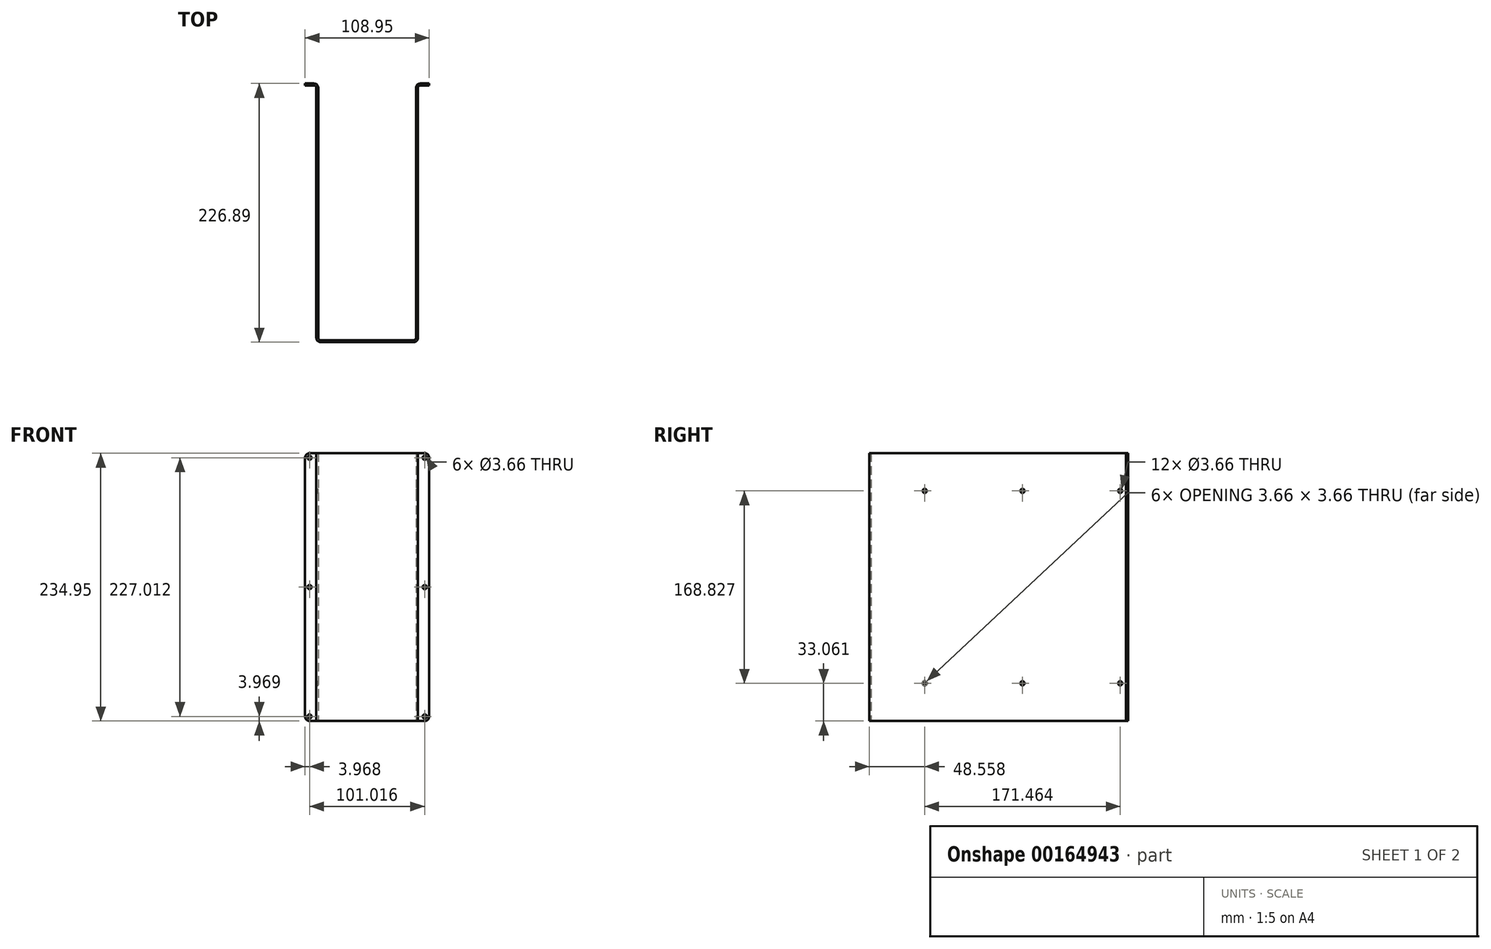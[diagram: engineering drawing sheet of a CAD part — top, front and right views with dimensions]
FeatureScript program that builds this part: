
annotation { "Feature Type Name" : "Feature", "Feature Type Description" : "" }
export const myFeature = defineFeature(function(context is Context, id is Id, definition is map)
    precondition{}
    {
        {
            var Q0;
            Q0=qCreatedBy(makeId("Top.planeOp"),FACE);
            var sketch = newSketch(context, id + "F0", { "sketchPlane" : qUnion([Q0])});
            skLineSegment(sketch, "E0", {"start": v(0, 0) * mm, "end": v(-11.63, 0) * mm});
            skLineSegment(sketch, "E1", {"start": v(0, 0) * mm, "end": v(0, -225.18) * mm});
            skLineSegment(sketch, "E2", {"start": v(0, -225.18) * mm, "end": v(85.7, -225.18) * mm});
            skLineSegment(sketch, "E3", {"start": v(87.4, -226.9) * mm, "end": v(-1.7, -226.9) * mm});
            skLineSegment(sketch, "E4", {"start": v(-1.7, -226.9) * mm, "end": v(-1.7, -1.7) * mm});
            skLineSegment(sketch, "E5", {"start": v(0, -225.18) * mm, "end": v(-1.7, -225.18) * mm, "construction": true});
            skLineSegment(sketch, "E6", {"start": v(42.85, -226.9) * mm, "end": v(42.85, -225.18) * mm, "construction": true});
            skLineSegment(sketch, "E7", {"start": v(85.7, -225.18) * mm, "end": v(85.7, 0) * mm});
            skLineSegment(sketch, "E8", {"start": v(85.7, 0) * mm, "end": v(97.32, 0) * mm});
            skLineSegment(sketch, "E9", {"start": v(87.4, -1.7) * mm, "end": v(87.4, -226.9) * mm});
            skLineSegment(sketch, "E10", {"start": v(97.32, 0) * mm, "end": v(97.32, -1.7) * mm});
            skLineSegment(sketch, "E11", {"start": v(97.32, -1.7) * mm, "end": v(87.4, -1.7) * mm});
            skLineSegment(sketch, "E12", {"start": v(-11.63, 0) * mm, "end": v(-11.63, -1.7) * mm});
            skLineSegment(sketch, "E13", {"start": v(-11.63, -1.7) * mm, "end": v(-1.7, -1.7) * mm});
            skSolve(sketch);
        }
        {
            var Q0;
            Q0=qSketchRegion(id+"F0",true);
            extrude(context, id + "F1", {"entities" : qUnion([Q0]), "depth" : 234.95 * mm});
        }
        {
            var Q0;
            Q0=makeQuery(id+"F1.opExtrude","SWEPT_EDGE",EDGE,{"disambiguationData":[OSD([sQuery(id+"F0.wireOp",EDGE,"E3"),sQuery(id+"F0.wireOp",EDGE,"E4")])]});
            var Q1;
            Q1=makeQuery(id+"F1.opExtrude","SWEPT_EDGE",EDGE,{"disambiguationData":[OSD([sQuery(id+"F0.wireOp",EDGE,"E3"),sQuery(id+"F0.wireOp",EDGE,"E9")])]});
            var Q2;
            Q2=makeQuery(id+"F1.opExtrude","SWEPT_EDGE",EDGE,{"disambiguationData":[OSD([sQuery(id+"F0.wireOp",EDGE,"E7"),sQuery(id+"F0.wireOp",EDGE,"E8")])]});
            var Q3;
            Q3=makeQuery(id+"F1.opExtrude","SWEPT_EDGE",EDGE,{"disambiguationData":[OSD([sQuery(id+"F0.wireOp",EDGE,"E0"),sQuery(id+"F0.wireOp",EDGE,"E1")])]});
            fillet(context, id + "F2", {"entities" : qUnion([Q0, Q1, Q2, Q3]), "radius" : 3.7 * mm, "tangentPropagation" : true, "allowEdgeOverflow" : false});
        }
        {
            var Q0;
            Q0=makeQuery(id+"F1.opExtrude","SWEPT_EDGE",EDGE,{"disambiguationData":[OSD([sQuery(id+"F0.wireOp",EDGE,"E1"),sQuery(id+"F0.wireOp",EDGE,"E2")])]});
            var Q1;
            Q1=makeQuery(id+"F1.opExtrude","SWEPT_EDGE",EDGE,{"disambiguationData":[OSD([sQuery(id+"F0.wireOp",EDGE,"E2"),sQuery(id+"F0.wireOp",EDGE,"E7")])]});
            var Q2;
            Q2=makeQuery(id+"F1.opExtrude","SWEPT_EDGE",EDGE,{"disambiguationData":[OSD([sQuery(id+"F0.wireOp",EDGE,"E4"),sQuery(id+"F0.wireOp",EDGE,"E13")])]});
            var Q3;
            Q3=makeQuery(id+"F1.opExtrude","SWEPT_EDGE",EDGE,{"disambiguationData":[OSD([sQuery(id+"F0.wireOp",EDGE,"E9"),sQuery(id+"F0.wireOp",EDGE,"E11")])]});
            fillet(context, id + "F3", {"entities" : qUnion([Q0, Q1, Q2, Q3]), "radius" : 1.98 * mm, "tangentPropagation" : true, "allowEdgeOverflow" : false});
        }
        {
            var Q0;
            Q0=makeQuery(id+"F1.opExtrude","CAP_EDGE",EDGE,{"disambiguationData":[OSD([sQuery(id+"F0.wireOp",EDGE,"E12")])],"isStart":true});
            var Q1;
            Q1=makeQuery(id+"F1.opExtrude","CAP_EDGE",EDGE,{"disambiguationData":[OSD([sQuery(id+"F0.wireOp",EDGE,"E12")])],"isStart":false});
            var Q2;
            Q2=makeQuery(id+"F1.opExtrude","CAP_EDGE",EDGE,{"disambiguationData":[OSD([sQuery(id+"F0.wireOp",EDGE,"E10")])],"isStart":false});
            var Q3;
            Q3=makeQuery(id+"F1.opExtrude","CAP_EDGE",EDGE,{"disambiguationData":[OSD([sQuery(id+"F0.wireOp",EDGE,"E10")])],"isStart":true});
            fillet(context, id + "F4", {"entities" : qUnion([Q0, Q1, Q2, Q3]), "radius" : 3.97 * mm, "tangentPropagation" : true, "allowEdgeOverflow" : false});
        }
        {
            var Q0;
            Q0=makeQuery(id+"F1.opExtrude","SWEPT_FACE",FACE,{"disambiguationData":[OSD([sQuery(id+"F0.wireOp",EDGE,"E9")])]});
            var sketch = newSketch(context, id + "F5", { "sketchPlane" : qUnion([Q0])});
            skLineSegment(sketch, "E14", {"start": v(-3.7, 117.48) * mm, "end": v(-92.6, 117.47) * mm, "construction": true});
            skLineSegment(sketch, "E15.bottom", {"start": v(-6.87, 33.06) * mm, "end": v(-178.33, 33.06) * mm, "construction": true});
            skLineSegment(sketch, "E15.top", {"start": v(-6.87, 201.89) * mm, "end": v(-178.33, 201.89) * mm, "construction": true});
            skLineSegment(sketch, "E15.left", {"start": v(-6.87, 33.06) * mm, "end": v(-6.87, 201.89) * mm, "construction": true});
            skLineSegment(sketch, "E15.right", {"start": v(-178.33, 33.06) * mm, "end": v(-178.33, 201.89) * mm, "construction": true});
            skPoint(sketch, "E15.middle", {"position": v(-92.6, 117.47) * mm});
            skLineSegment(sketch, "E16", {"start": v(-6.87, 33.06) * mm, "end": v(-3.7, 33.06) * mm, "construction": true});
            skCircle(sketch, "E17", {"center": v(-6.87, 33.06) * mm, "radius": 1.83 * mm});
            skCircle(sketch, "E18", {"center": v(-92.6, 33.06) * mm, "radius": 1.83 * mm});
            skCircle(sketch, "E19", {"center": v(-178.33, 33.06) * mm, "radius": 1.83 * mm});
            skCircle(sketch, "E20", {"center": v(-178.33, 201.89) * mm, "radius": 1.83 * mm});
            skCircle(sketch, "E21", {"center": v(-92.6, 201.89) * mm, "radius": 1.83 * mm});
            skCircle(sketch, "E22", {"center": v(-6.87, 201.89) * mm, "radius": 1.83 * mm});
            skSolve(sketch);
        }
        {
            var Q0;
            Q0 = qSketchRegion(id + "F5", true);
            var Q1;
            Q1=makeQuery(id+"F1.opExtrude","SWEPT_FACE",FACE,{"disambiguationData":[OSD([sQuery(id+"F0.wireOp",EDGE,"E4")])]});
            extrude(context, id + "F6", {"entities" : qUnion([Q0]), "operationType" : NewBodyOperationType.REMOVE, "endBound" : BoundingType.UP_TO_SURFACE, "oppositeDirection" : true, "endBoundEntityFace" : qUnion([Q1]), "depth" : 25.4 * mm});
        }
        {
            var Q0;
            Q0=makeQuery(id+"F1.opExtrude","SWEPT_FACE",FACE,{"disambiguationData":[OSD([sQuery(id+"F0.wireOp",EDGE,"E8")])]});
            var sketch = newSketch(context, id + "F7", { "sketchPlane" : qUnion([Q0])});
            skLineSegment(sketch, "E23", {"start": v(-89.39, 117.48) * mm, "end": v(3.7, 117.48) * mm, "construction": true});
            skLineSegment(sketch, "E24.bottom", {"start": v(-93.35, 230.98) * mm, "end": v(7.66, 230.98) * mm, "construction": true});
            skLineSegment(sketch, "E24.top", {"start": v(-93.35, 3.97) * mm, "end": v(7.66, 3.97) * mm, "construction": true});
            skLineSegment(sketch, "E24.left", {"start": v(-93.35, 230.98) * mm, "end": v(-93.35, 3.97) * mm, "construction": true});
            skLineSegment(sketch, "E24.right", {"start": v(7.66, 230.98) * mm, "end": v(7.66, 3.97) * mm, "construction": true});
            skPoint(sketch, "E24.middle", {"position": v(-42.85, 117.48) * mm});
            skCircle(sketch, "E25", {"center": v(-93.35, 3.97) * mm, "radius": 1.83 * mm});
            skCircle(sketch, "E26", {"center": v(-93.35, 117.48) * mm, "radius": 1.83 * mm});
            skCircle(sketch, "E27", {"center": v(-93.35, 230.98) * mm, "radius": 1.83 * mm});
            skCircle(sketch, "E28", {"center": v(7.66, 230.98) * mm, "radius": 1.83 * mm});
            skCircle(sketch, "E29", {"center": v(7.66, 117.48) * mm, "radius": 1.83 * mm});
            skCircle(sketch, "E30", {"center": v(7.66, 3.97) * mm, "radius": 1.83 * mm});
            skSolve(sketch);
        }
        {
            var Q0;
            Q0 = qSketchRegion(id + "F7", true);
            var Q1;
            Q1=makeQuery(id+"F1.opExtrude","SWEPT_FACE",FACE,{"disambiguationData":[OSD([sQuery(id+"F0.wireOp",EDGE,"E11")])]});
            extrude(context, id + "F8", {"entities" : qUnion([Q0]), "operationType" : NewBodyOperationType.REMOVE, "endBound" : BoundingType.UP_TO_SURFACE, "oppositeDirection" : true, "endBoundEntityFace" : qUnion([Q1]), "depth" : 25.4 * mm});
        }
    });
